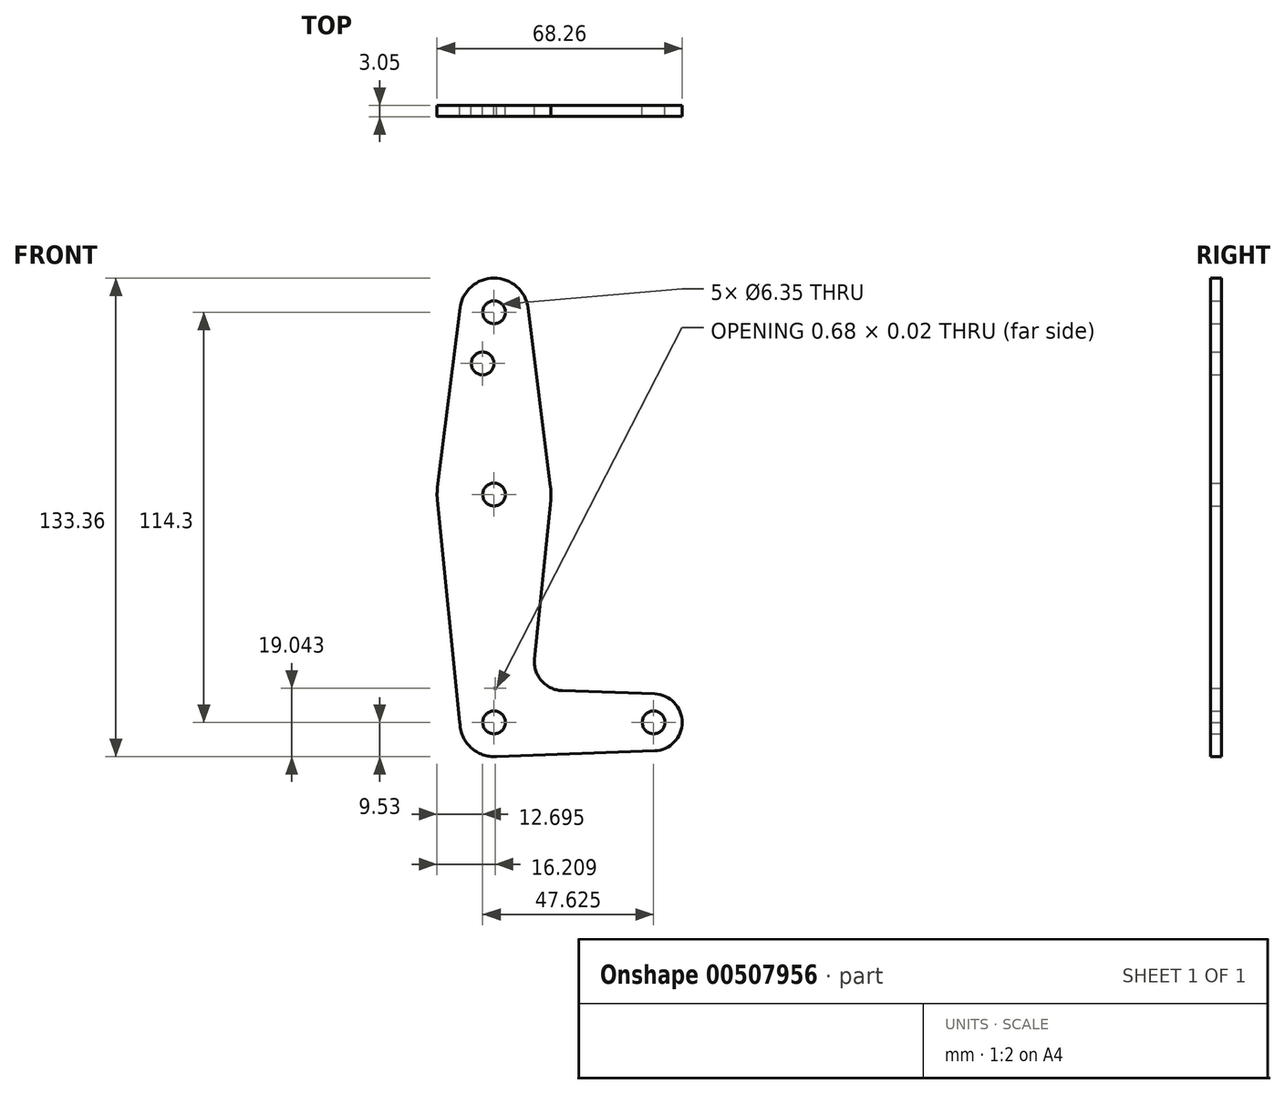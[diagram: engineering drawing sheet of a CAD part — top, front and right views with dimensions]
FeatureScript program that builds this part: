
annotation { "Feature Type Name" : "Feature", "Feature Type Description" : "" }
export const myFeature = defineFeature(function(context is Context, id is Id, definition is map)
    precondition{}
    {
        {
            var Q0;
            Q0=qCreatedBy(makeId("Front.planeOp"),FACE);
            var sketch = newSketch(context, id + "F0", { "sketchPlane" : qUnion([Q0])});
            skCircle(sketch, "E0", {"center": v(0, 0) * mm, "radius": 9.53 * mm});
            skCircle(sketch, "E1", {"center": v(0, 63.5) * mm, "radius": 15.88 * mm});
            skCircle(sketch, "E2", {"center": v(0, 114.3) * mm, "radius": 9.53 * mm});
            skCircle(sketch, "E3", {"center": v(44.45, 0) * mm, "radius": 7.94 * mm});
            skLineSegment(sketch, "E4", {"start": v(0, 0) * mm, "end": v(0, 114.3) * mm, "construction": true});
            skLineSegment(sketch, "E5", {"start": v(0, 0) * mm, "end": v(44.45, 0) * mm, "construction": true});
            skLineSegment(sketch, "E6", {"start": v(-9.52, 0) * mm, "end": v(-15.8, 61.9) * mm});
            skLineSegment(sketch, "E7", {"start": v(11.3, 17.6) * mm, "end": v(15.8, 61.9) * mm});
            skLineSegment(sketch, "E8", {"start": v(0, 9.53) * mm, "end": v(0.68, 9.5) * mm});
            skLineSegment(sketch, "E9", {"start": v(0, -9.53) * mm, "end": v(44.73, -7.93) * mm});
            skLineSegment(sketch, "E10", {"start": v(-9.45, 115.5) * mm, "end": v(-15.75, 65.48) * mm});
            skLineSegment(sketch, "E11", {"start": v(9.45, 115.5) * mm, "end": v(15.75, 65.48) * mm});
            skCircle(sketch, "E12", {"center": v(0, 114.3) * mm, "radius": 3.18 * mm});
            skCircle(sketch, "E13", {"center": v(-3.18, 100.03) * mm, "radius": 3.18 * mm});
            skCircle(sketch, "E14", {"center": v(0, 63.5) * mm, "radius": 3.18 * mm});
            skCircle(sketch, "E15", {"center": v(0, 0) * mm, "radius": 3.18 * mm});
            skCircle(sketch, "E16", {"center": v(44.45, 0) * mm, "radius": 3.18 * mm});
            skLineSegment(sketch, "E17.trimOffspring", {"start": v(18.93, 8.85) * mm, "end": v(44.73, 7.93) * mm});
            skPoint(sketch, "E18.visualSharp", {"position": v(10.45, 9.15) * mm});
            skArc(sketch, "E18.filletArc", {"start": v(11.3, 17.6) * mm, "mid": v(13.22, 11.57) * mm, "end": v(18.93, 8.85) * mm});
            skSolve(sketch);
        }
        {
            var Q0;
            Q0 = qSketchRegion(id + "F0", true);
            extrude(context, id + "F1", {"entities" : qUnion([Q0]), "depth" : 3.05 * mm, "offsetDistance" : 25.4 * mm});
        }
    });
